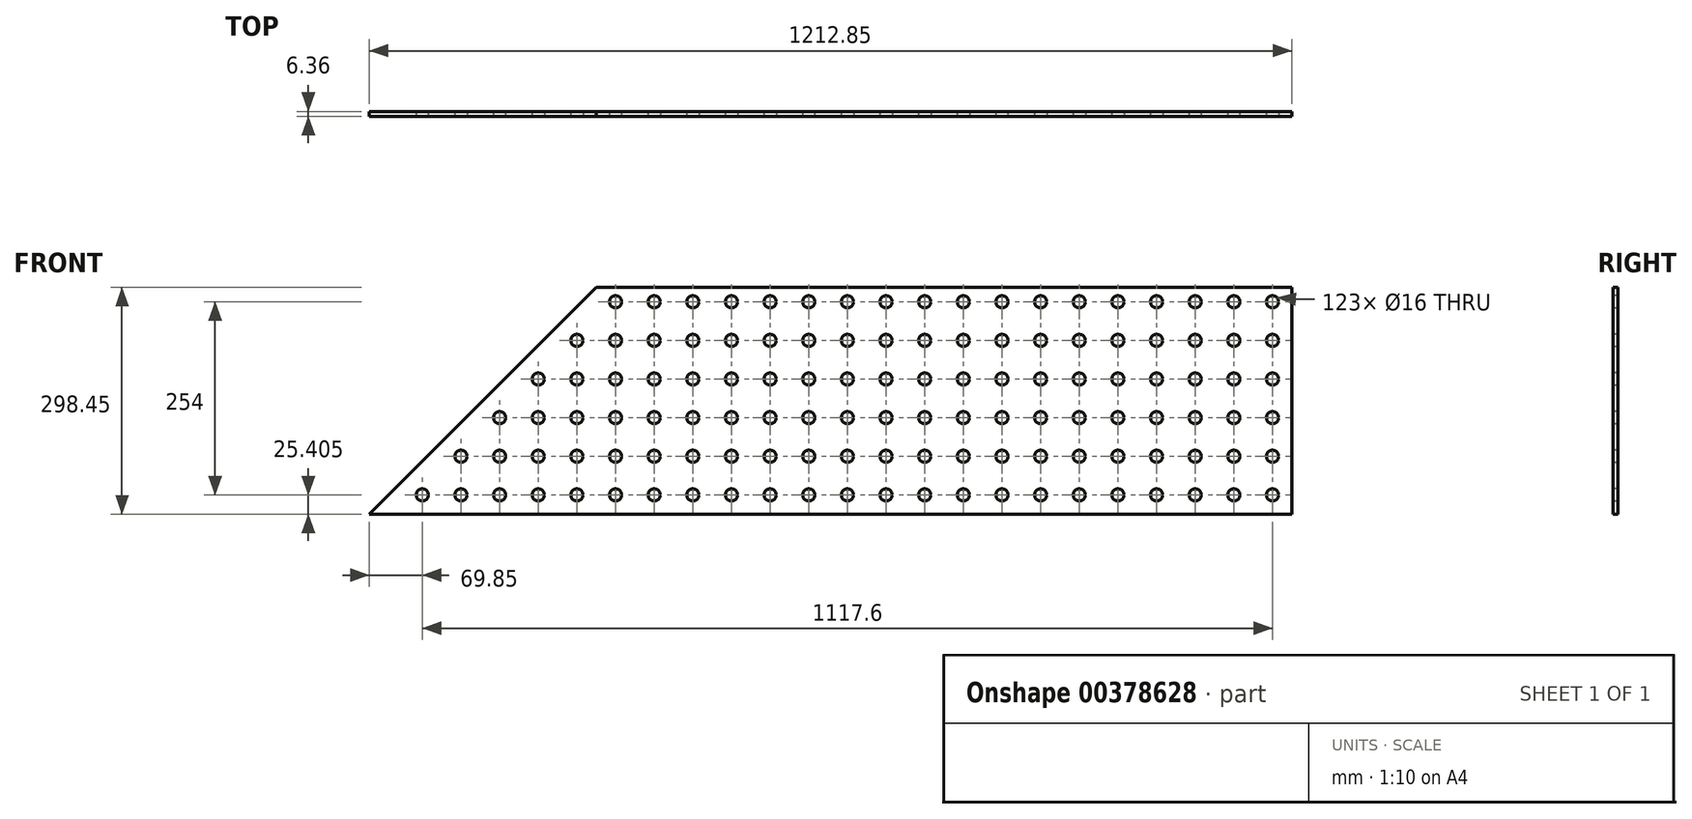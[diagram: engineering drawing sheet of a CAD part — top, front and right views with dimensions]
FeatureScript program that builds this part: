
annotation { "Feature Type Name" : "Feature", "Feature Type Description" : "" }
export const myFeature = defineFeature(function(context is Context, id is Id, definition is map)
    precondition{}
    {
        {
            var Q0;
            Q0=qCreatedBy(makeId("Front.planeOp"),FACE);
            var sketch = newSketch(context, id + "F0", { "sketchPlane" : qUnion([Q0])});
            skLineSegment(sketch, "E0.bottom", {"start": v(457.2, 149.22) * mm, "end": v(-457.2, 149.22) * mm});
            skLineSegment(sketch, "E0.top", {"start": v(457.2, -149.23) * mm, "end": v(-457.2, -149.23) * mm});
            skLineSegment(sketch, "E0.left", {"start": v(457.2, 149.22) * mm, "end": v(457.2, -149.23) * mm});
            skLineSegment(sketch, "E0.right", {"start": v(-457.2, 149.22) * mm, "end": v(-457.2, -149.23) * mm, "construction": true});
            skPoint(sketch, "E0.middle", {"position": v(0, 0) * mm});
            skLineSegment(sketch, "E1", {"start": v(-457.2, -149.23) * mm, "end": v(-755.65, -149.23) * mm});
            skLineSegment(sketch, "E2", {"start": v(-755.65, -149.23) * mm, "end": v(-457.2, 149.23) * mm});
            skSolve(sketch);
        }
        {
            var Q0;
            Q0 = qSketchRegion(id + "F0", true);
            extrude(context, id + "F1", {"entities" : qUnion([Q0]), "endBound" : BoundingType.SYMMETRIC, "depth" : 6.35 * mm});
        }
        {
            var Q0;
            Q0=makeQuery(id+"F1.opExtrude","CAP_FACE",FACE,{"disambiguationData":[OSD([sQuery(id+"F0.wireOp",EDGE,"E0.bottom"),sQuery(id+"F0.wireOp",EDGE,"E0.top"),sQuery(id+"F0.wireOp",EDGE,"E0.left"),sQuery(id+"F0.wireOp",EDGE,"E1"),sQuery(id+"F0.wireOp",EDGE,"E2")])],"isStart":false});
            var sketch = newSketch(context, id + "F2", { "sketchPlane" : qUnion([Q0])});
            skCircle(sketch, "E3", {"center": v(431.8, -123.83) * mm, "radius": 8 * mm});
            skCircle(sketch, "E4.0.1.0", {"center": v(431.8, -73.03) * mm, "radius": 8 * mm});
            skCircle(sketch, "E4.1.0.0", {"center": v(381, -123.83) * mm, "radius": 8 * mm});
            skCircle(sketch, "E4.1.1.0", {"center": v(381, -73.03) * mm, "radius": 8 * mm});
            skCircle(sketch, "E4.2.0.0", {"center": v(330.2, -123.83) * mm, "radius": 8 * mm});
            skCircle(sketch, "E4.2.1.0", {"center": v(330.2, -73.03) * mm, "radius": 8 * mm});
            skCircle(sketch, "E4.3.0.0", {"center": v(279.4, -123.83) * mm, "radius": 8 * mm});
            skCircle(sketch, "E4.3.1.0", {"center": v(279.4, -73.03) * mm, "radius": 8 * mm});
            skCircle(sketch, "E4.4.0.0", {"center": v(228.6, -123.83) * mm, "radius": 8 * mm});
            skCircle(sketch, "E4.4.1.0", {"center": v(228.6, -73.03) * mm, "radius": 8 * mm});
            skCircle(sketch, "E4.5.0.0", {"center": v(177.8, -123.83) * mm, "radius": 8 * mm});
            skCircle(sketch, "E4.5.1.0", {"center": v(177.8, -73.03) * mm, "radius": 8 * mm});
            skCircle(sketch, "E4.6.0.0", {"center": v(127, -123.83) * mm, "radius": 8 * mm});
            skCircle(sketch, "E4.6.1.0", {"center": v(127, -73.03) * mm, "radius": 8 * mm});
            skCircle(sketch, "E4.7.0.0", {"center": v(76.2, -123.83) * mm, "radius": 8 * mm});
            skCircle(sketch, "E4.7.1.0", {"center": v(76.2, -73.03) * mm, "radius": 8 * mm});
            skCircle(sketch, "E4.8.0.0", {"center": v(25.4, -123.83) * mm, "radius": 8 * mm});
            skCircle(sketch, "E4.8.1.0", {"center": v(25.4, -73.03) * mm, "radius": 8 * mm});
            skCircle(sketch, "E4.9.0.0", {"center": v(-25.4, -123.83) * mm, "radius": 8 * mm});
            skCircle(sketch, "E4.9.1.0", {"center": v(-25.4, -73.03) * mm, "radius": 8 * mm});
            skCircle(sketch, "E4.10.0.0", {"center": v(-76.2, -123.83) * mm, "radius": 8 * mm});
            skCircle(sketch, "E4.10.1.0", {"center": v(-76.2, -73.03) * mm, "radius": 8 * mm});
            skCircle(sketch, "E4.11.0.0", {"center": v(-127, -123.83) * mm, "radius": 8 * mm});
            skCircle(sketch, "E4.11.1.0", {"center": v(-127, -73.03) * mm, "radius": 8 * mm});
            skCircle(sketch, "E4.12.0.0", {"center": v(-177.8, -123.83) * mm, "radius": 8 * mm});
            skCircle(sketch, "E4.12.1.0", {"center": v(-177.8, -73.03) * mm, "radius": 8 * mm});
            skCircle(sketch, "E4.13.0.0", {"center": v(-228.6, -123.83) * mm, "radius": 8 * mm});
            skCircle(sketch, "E4.13.1.0", {"center": v(-228.6, -73.03) * mm, "radius": 8 * mm});
            skCircle(sketch, "E4.14.0.0", {"center": v(-279.4, -123.83) * mm, "radius": 8 * mm});
            skCircle(sketch, "E4.14.1.0", {"center": v(-279.4, -73.03) * mm, "radius": 8 * mm});
            skCircle(sketch, "E4.15.0.0", {"center": v(-330.2, -123.83) * mm, "radius": 8 * mm});
            skCircle(sketch, "E4.15.1.0", {"center": v(-330.2, -73.03) * mm, "radius": 8 * mm});
            skCircle(sketch, "E4.16.0.0", {"center": v(-381, -123.83) * mm, "radius": 8 * mm});
            skCircle(sketch, "E4.16.1.0", {"center": v(-381, -73.03) * mm, "radius": 8 * mm});
            skCircle(sketch, "E4.17.0.0", {"center": v(-431.8, -123.83) * mm, "radius": 8 * mm});
            skCircle(sketch, "E4.17.1.0", {"center": v(-431.8, -73.03) * mm, "radius": 8 * mm});
            skCircle(sketch, "E4.18.0.0", {"center": v(-482.6, -123.83) * mm, "radius": 8 * mm});
            skCircle(sketch, "E4.18.1.0", {"center": v(-482.6, -73.03) * mm, "radius": 8 * mm});
            skCircle(sketch, "E4.19.0.0", {"center": v(-533.4, -123.83) * mm, "radius": 8 * mm});
            skCircle(sketch, "E4.19.1.0", {"center": v(-533.4, -73.03) * mm, "radius": 8 * mm});
            skLineSegment(sketch, "E4.direction1", {"start": v(431.8, -123.83) * mm, "end": v(381, -123.83) * mm, "construction": true});
            skLineSegment(sketch, "E4.direction2", {"start": v(431.8, -123.83) * mm, "end": v(431.8, -73.03) * mm, "construction": true});
            skCircle(sketch, "E5.0.0.2", {"center": v(431.8, -22.23) * mm, "radius": 8 * mm});
            skCircle(sketch, "E5.0.0.3", {"center": v(431.8, 28.57) * mm, "radius": 8 * mm});
            skCircle(sketch, "E5.0.0.4", {"center": v(431.8, 79.37) * mm, "radius": 8 * mm});
            skCircle(sketch, "E5.0.0.5", {"center": v(431.8, 130.17) * mm, "radius": 8 * mm});
            skCircle(sketch, "E5.0.1.2", {"center": v(381, -22.23) * mm, "radius": 8 * mm});
            skCircle(sketch, "E5.0.1.3", {"center": v(381, 28.57) * mm, "radius": 8 * mm});
            skCircle(sketch, "E5.0.1.4", {"center": v(381, 79.37) * mm, "radius": 8 * mm});
            skCircle(sketch, "E5.0.1.5", {"center": v(381, 130.17) * mm, "radius": 8 * mm});
            skCircle(sketch, "E5.0.2.2", {"center": v(330.2, -22.23) * mm, "radius": 8 * mm});
            skCircle(sketch, "E5.0.2.3", {"center": v(330.2, 28.57) * mm, "radius": 8 * mm});
            skCircle(sketch, "E5.0.2.4", {"center": v(330.2, 79.37) * mm, "radius": 8 * mm});
            skCircle(sketch, "E5.0.2.5", {"center": v(330.2, 130.17) * mm, "radius": 8 * mm});
            skCircle(sketch, "E5.0.3.2", {"center": v(279.4, -22.23) * mm, "radius": 8 * mm});
            skCircle(sketch, "E5.0.3.3", {"center": v(279.4, 28.57) * mm, "radius": 8 * mm});
            skCircle(sketch, "E5.0.3.4", {"center": v(279.4, 79.37) * mm, "radius": 8 * mm});
            skCircle(sketch, "E5.0.3.5", {"center": v(279.4, 130.17) * mm, "radius": 8 * mm});
            skCircle(sketch, "E5.0.4.2", {"center": v(228.6, -22.23) * mm, "radius": 8 * mm});
            skCircle(sketch, "E5.0.4.3", {"center": v(228.6, 28.57) * mm, "radius": 8 * mm});
            skCircle(sketch, "E5.0.4.4", {"center": v(228.6, 79.37) * mm, "radius": 8 * mm});
            skCircle(sketch, "E5.0.4.5", {"center": v(228.6, 130.17) * mm, "radius": 8 * mm});
            skCircle(sketch, "E5.0.5.2", {"center": v(177.8, -22.23) * mm, "radius": 8 * mm});
            skCircle(sketch, "E5.0.5.3", {"center": v(177.8, 28.57) * mm, "radius": 8 * mm});
            skCircle(sketch, "E5.0.5.4", {"center": v(177.8, 79.37) * mm, "radius": 8 * mm});
            skCircle(sketch, "E5.0.5.5", {"center": v(177.8, 130.17) * mm, "radius": 8 * mm});
            skCircle(sketch, "E5.0.6.2", {"center": v(127, -22.23) * mm, "radius": 8 * mm});
            skCircle(sketch, "E5.0.6.3", {"center": v(127, 28.57) * mm, "radius": 8 * mm});
            skCircle(sketch, "E5.0.6.4", {"center": v(127, 79.37) * mm, "radius": 8 * mm});
            skCircle(sketch, "E5.0.6.5", {"center": v(127, 130.17) * mm, "radius": 8 * mm});
            skCircle(sketch, "E5.0.7.2", {"center": v(76.2, -22.23) * mm, "radius": 8 * mm});
            skCircle(sketch, "E5.0.7.3", {"center": v(76.2, 28.57) * mm, "radius": 8 * mm});
            skCircle(sketch, "E5.0.7.4", {"center": v(76.2, 79.37) * mm, "radius": 8 * mm});
            skCircle(sketch, "E5.0.7.5", {"center": v(76.2, 130.17) * mm, "radius": 8 * mm});
            skCircle(sketch, "E5.0.8.2", {"center": v(25.4, -22.23) * mm, "radius": 8 * mm});
            skCircle(sketch, "E5.0.8.3", {"center": v(25.4, 28.57) * mm, "radius": 8 * mm});
            skCircle(sketch, "E5.0.8.4", {"center": v(25.4, 79.37) * mm, "radius": 8 * mm});
            skCircle(sketch, "E5.0.8.5", {"center": v(25.4, 130.17) * mm, "radius": 8 * mm});
            skCircle(sketch, "E5.0.9.2", {"center": v(-25.4, -22.23) * mm, "radius": 8 * mm});
            skCircle(sketch, "E5.0.9.3", {"center": v(-25.4, 28.57) * mm, "radius": 8 * mm});
            skCircle(sketch, "E5.0.9.4", {"center": v(-25.4, 79.37) * mm, "radius": 8 * mm});
            skCircle(sketch, "E5.0.9.5", {"center": v(-25.4, 130.17) * mm, "radius": 8 * mm});
            skCircle(sketch, "E5.0.10.2", {"center": v(-76.2, -22.23) * mm, "radius": 8 * mm});
            skCircle(sketch, "E5.0.10.3", {"center": v(-76.2, 28.57) * mm, "radius": 8 * mm});
            skCircle(sketch, "E5.0.10.4", {"center": v(-76.2, 79.37) * mm, "radius": 8 * mm});
            skCircle(sketch, "E5.0.10.5", {"center": v(-76.2, 130.17) * mm, "radius": 8 * mm});
            skCircle(sketch, "E5.0.11.2", {"center": v(-127, -22.23) * mm, "radius": 8 * mm});
            skCircle(sketch, "E5.0.11.3", {"center": v(-127, 28.57) * mm, "radius": 8 * mm});
            skCircle(sketch, "E5.0.11.4", {"center": v(-127, 79.37) * mm, "radius": 8 * mm});
            skCircle(sketch, "E5.0.11.5", {"center": v(-127, 130.17) * mm, "radius": 8 * mm});
            skCircle(sketch, "E5.0.12.2", {"center": v(-177.8, -22.23) * mm, "radius": 8 * mm});
            skCircle(sketch, "E5.0.12.3", {"center": v(-177.8, 28.57) * mm, "radius": 8 * mm});
            skCircle(sketch, "E5.0.12.4", {"center": v(-177.8, 79.37) * mm, "radius": 8 * mm});
            skCircle(sketch, "E5.0.12.5", {"center": v(-177.8, 130.17) * mm, "radius": 8 * mm});
            skCircle(sketch, "E5.0.13.2", {"center": v(-228.6, -22.23) * mm, "radius": 8 * mm});
            skCircle(sketch, "E5.0.13.3", {"center": v(-228.6, 28.57) * mm, "radius": 8 * mm});
            skCircle(sketch, "E5.0.13.4", {"center": v(-228.6, 79.37) * mm, "radius": 8 * mm});
            skCircle(sketch, "E5.0.13.5", {"center": v(-228.6, 130.17) * mm, "radius": 8 * mm});
            skCircle(sketch, "E5.0.14.2", {"center": v(-279.4, -22.23) * mm, "radius": 8 * mm});
            skCircle(sketch, "E5.0.14.3", {"center": v(-279.4, 28.57) * mm, "radius": 8 * mm});
            skCircle(sketch, "E5.0.14.4", {"center": v(-279.4, 79.37) * mm, "radius": 8 * mm});
            skCircle(sketch, "E5.0.14.5", {"center": v(-279.4, 130.17) * mm, "radius": 8 * mm});
            skCircle(sketch, "E5.0.15.2", {"center": v(-330.2, -22.23) * mm, "radius": 8 * mm});
            skCircle(sketch, "E5.0.15.3", {"center": v(-330.2, 28.57) * mm, "radius": 8 * mm});
            skCircle(sketch, "E5.0.15.4", {"center": v(-330.2, 79.37) * mm, "radius": 8 * mm});
            skCircle(sketch, "E5.0.15.5", {"center": v(-330.2, 130.17) * mm, "radius": 8 * mm});
            skCircle(sketch, "E5.0.16.2", {"center": v(-381, -22.23) * mm, "radius": 8 * mm});
            skCircle(sketch, "E5.0.16.3", {"center": v(-381, 28.57) * mm, "radius": 8 * mm});
            skCircle(sketch, "E5.0.16.4", {"center": v(-381, 79.37) * mm, "radius": 8 * mm});
            skCircle(sketch, "E5.0.16.5", {"center": v(-381, 130.17) * mm, "radius": 8 * mm});
            skCircle(sketch, "E5.0.17.2", {"center": v(-431.8, -22.23) * mm, "radius": 8 * mm});
            skCircle(sketch, "E5.0.17.3", {"center": v(-431.8, 28.57) * mm, "radius": 8 * mm});
            skCircle(sketch, "E5.0.17.4", {"center": v(-431.8, 79.37) * mm, "radius": 8 * mm});
            skCircle(sketch, "E5.0.17.5", {"center": v(-431.8, 130.17) * mm, "radius": 8 * mm});
            skCircle(sketch, "E5.0.18.2", {"center": v(-482.6, -22.23) * mm, "radius": 8 * mm});
            skCircle(sketch, "E5.0.18.3", {"center": v(-482.6, 28.57) * mm, "radius": 8 * mm});
            skCircle(sketch, "E5.0.18.4", {"center": v(-482.6, 79.37) * mm, "radius": 8 * mm});
            skCircle(sketch, "E5.0.19.2", {"center": v(-533.4, -22.23) * mm, "radius": 8 * mm});
            skCircle(sketch, "E5.0.19.3", {"center": v(-533.4, 28.57) * mm, "radius": 8 * mm});
            skCircle(sketch, "E6.0.20.0", {"center": v(-584.2, -123.83) * mm, "radius": 8 * mm});
            skCircle(sketch, "E6.0.20.1", {"center": v(-584.2, -73.03) * mm, "radius": 8 * mm});
            skCircle(sketch, "E6.0.20.2", {"center": v(-584.2, -22.23) * mm, "radius": 8 * mm});
            skCircle(sketch, "E6.0.21.0", {"center": v(-635, -123.83) * mm, "radius": 8 * mm});
            skCircle(sketch, "E6.0.21.1", {"center": v(-635, -73.03) * mm, "radius": 8 * mm});
            skCircle(sketch, "E6.0.22.0", {"center": v(-685.8, -123.83) * mm, "radius": 8 * mm});
            skSolve(sketch);
        }
        {
            var Q0;
            Q0 = qSketchRegion(id + "F2", true);
            extrude(context, id + "F3", {"entities" : qUnion([Q0]), "operationType" : NewBodyOperationType.REMOVE, "endBound" : BoundingType.THROUGH_ALL, "oppositeDirection" : true, "depth" : 25.4 * mm});
        }
    });
